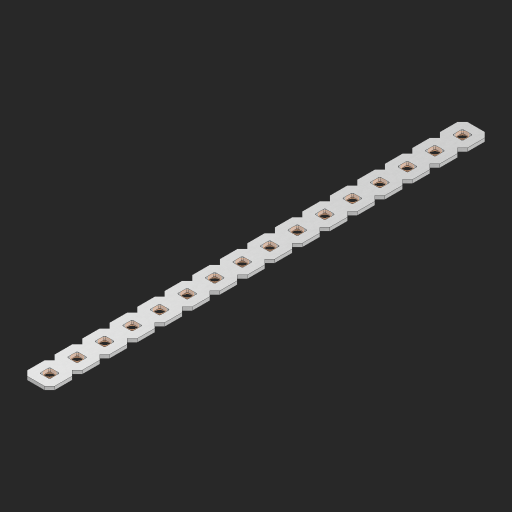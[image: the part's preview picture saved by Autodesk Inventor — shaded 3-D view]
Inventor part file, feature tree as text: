
AUTODESK INVENTOR PART (.ipt)
format: ipt  version: 2023 (Build 270158000, 158)  size: 441,856 bytes
history: native  units: in
note: dims shown in document units (in); Inventor stores cm internally (conversion verified against a paired STEP export)
features: other x17, extrude x15, sketch x2, pattern_linear x1
ambient origin geometry x8: Origin, YZ Plane, XZ Plane, XY Plane, X Axis, Y Axis, Z Axis, Center Point
bodies: Solid1 (feature_tree), Body (feature_tree)
feature tree (35):
  pattern_linear  "Rectangular Pattern1"  Spacing1=0.09in  [1 undecoded]
  sketch  "Sketch1"  dims[d1=0.5in]
  sketch  "Sketch2"  dims[d2=0.182in d3=0.09in d4=0.09in d5=0.09in d6=0.09in d7=0.09in d8=0.09in d9=0.09in d10=0.09in d11=0.02in d13=0.0in d14=0.172in d15=0.0625in d16=0.0in d19=0.5in d22=0.5in]
  other  "Srf1"
  other  "Srf126"
  other  "Srf127"
  other  "Srf128"
  other  "Srf129"
  other  "Srf130"
  other  "Srf131"
  other  "Srf250"
  other  "Srf251"
  other  "Srf252"
  other  "Srf253"
  other  "Srf254"
  other  "Srf255"
  other  "Srf256"
  other  "Srf257"
  other  "Srf258"
  other  "Circle"
  extrude  "ExtrusionSrf126"  Depth=0.09in
  extrude  "ExtrusionSrf127"  Depth=0.09in
  extrude  "ExtrusionSrf128"  Depth=0.09in
  extrude  "ExtrusionSrf129"  Depth=0.09in
  extrude  "ExtrusionSrf130"  Depth=0.09in
  extrude  "ExtrusionSrf131"  Depth=0.09in
  extrude  "ExtrusionSrf250"  Depth=0.09in
  extrude  "ExtrusionSrf251"  Depth=0.02in
  extrude  "ExtrusionSrf252"  TaperAngle=0.0deg  [1 undecoded]
  extrude  "ExtrusionSrf253"  Depth=0.5in
  extrude  "ExtrusionSrf254"  Depth=0.0625in TaperAngle=0.0deg
  extrude  "ExtrusionSrf255"  Depth=0.5in
  extrude  "ExtrusionSrf256"  Depth=0.5in
  extrude  "ExtrusionSrf257"  [1 undecoded]
  extrude  "ExtrusionSrf258"  [1 undecoded]
note: 4 required parameter values undecoded (feature->parameter linkage not recoverable at this tier; creation-order binding heuristic only, values carry confidence <= 0.55)
